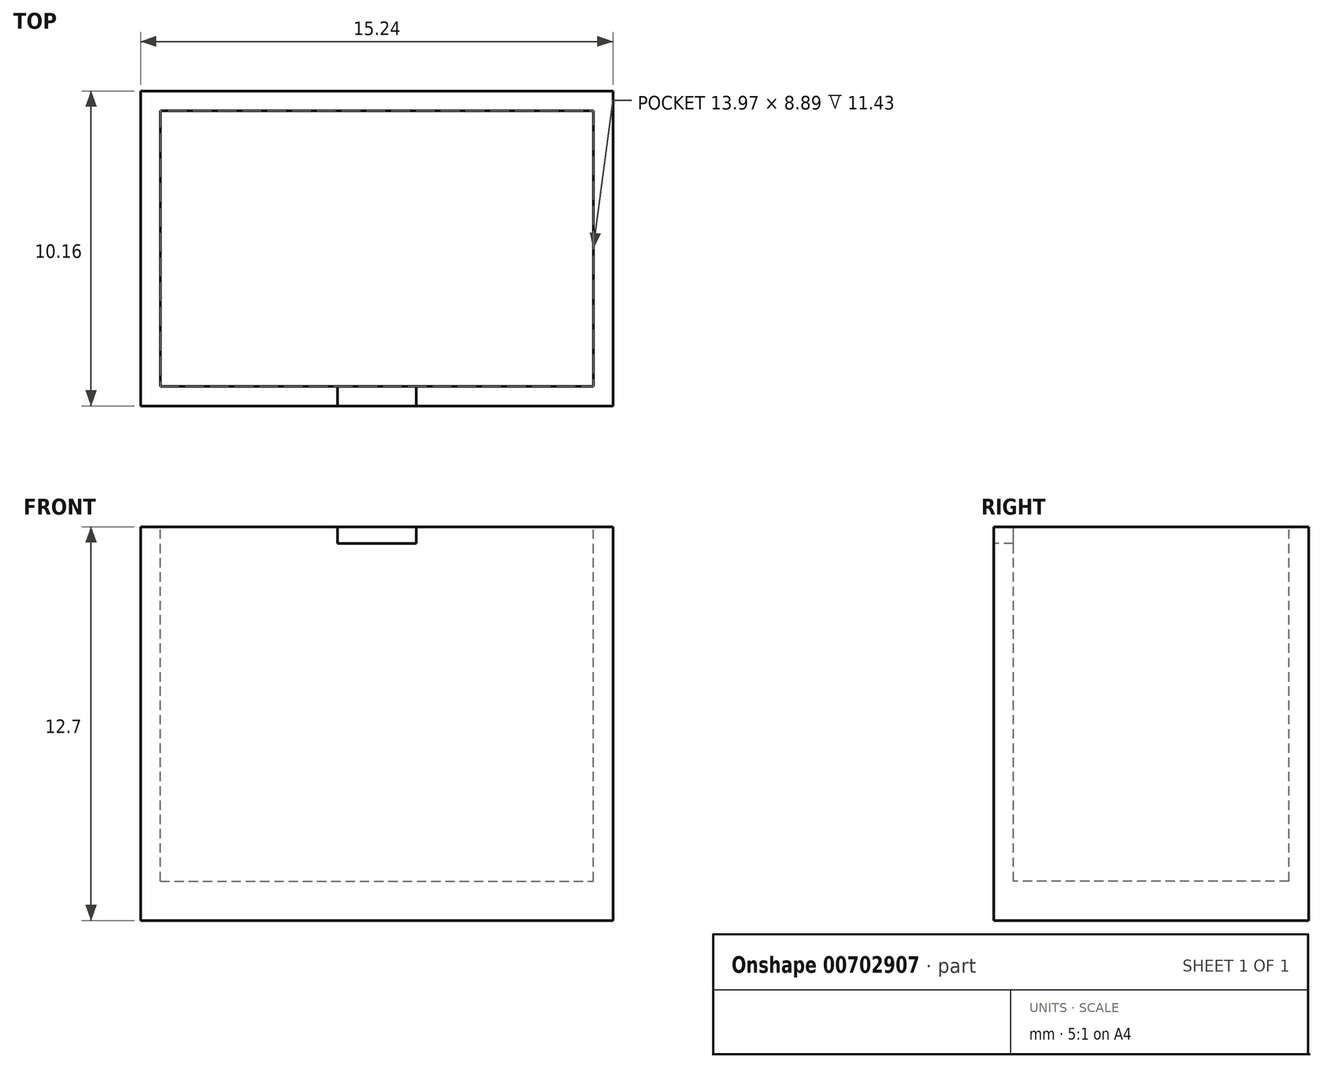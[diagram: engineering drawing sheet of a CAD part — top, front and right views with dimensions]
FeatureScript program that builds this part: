
annotation { "Feature Type Name" : "Feature", "Feature Type Description" : "" }
export const myFeature = defineFeature(function(context is Context, id is Id, definition is map)
    precondition{}
    {
        {
            var Q0;
            Q0=qCreatedBy(makeId("Top.planeOp"),FACE);
            var sketch = newSketch(context, id + "F0", { "sketchPlane" : qUnion([Q0])});
            skLineSegment(sketch, "E0.bottom", {"start": v(-7.62, 5.08) * mm, "end": v(7.62, 5.08) * mm});
            skLineSegment(sketch, "E0.top", {"start": v(-7.62, -5.08) * mm, "end": v(7.62, -5.08) * mm});
            skLineSegment(sketch, "E0.left", {"start": v(-7.62, 5.08) * mm, "end": v(-7.62, -5.08) * mm});
            skLineSegment(sketch, "E0.right", {"start": v(7.62, 5.08) * mm, "end": v(7.62, -5.08) * mm});
            skPoint(sketch, "E0.middle", {"position": v(0, 0) * mm});
            skSolve(sketch);
        }
        {
            var Q0;
            Q0=makeQuery(id+"F0.imprint","IMPRINT",FACE,{"disambiguationData":[TD([[makeQuery(id+"F0.imprint","IMPRINT",EDGE,{"derivedFrom":sQuery(id+"F0.wireOp",EDGE,"E0.bottom")}),-1.0]])]});
            extrude(context, id + "F1", {"entities" : qUnion([Q0]), "depth" : 12.7 * mm, "offsetDistance" : 25.4 * mm});
        }
        {
            var Q0;
            Q0=makeQuery(id+"F1.opExtrude","CAP_FACE",FACE,{"disambiguationData":[OSD([sQuery(id+"F0.wireOp",EDGE,"E0.bottom"),sQuery(id+"F0.wireOp",EDGE,"E0.top"),sQuery(id+"F0.wireOp",EDGE,"E0.left"),sQuery(id+"F0.wireOp",EDGE,"E0.right")])],"isStart":false});
            var sketch = newSketch(context, id + "F2", { "sketchPlane" : qUnion([Q0])});
            skLineSegment(sketch, "E1.bottom", {"start": v(-6.99, 4.45) * mm, "end": v(6.99, 4.45) * mm});
            skLineSegment(sketch, "E1.top", {"start": v(-6.98, -4.45) * mm, "end": v(6.98, -4.45) * mm});
            skLineSegment(sketch, "E1.left", {"start": v(-6.99, 4.45) * mm, "end": v(-6.99, -4.44) * mm});
            skLineSegment(sketch, "E1.right", {"start": v(6.99, 4.45) * mm, "end": v(6.99, -4.44) * mm});
            skPoint(sketch, "E1.middle", {"position": v(0, 0) * mm});
            skSolve(sketch);
        }
        {
            var Q0;
            Q0=makeQuery(id+"F2.imprint","IMPRINT",FACE,{"disambiguationData":[TD([[makeQuery(id+"F2.imprint","IMPRINT",EDGE,{"derivedFrom":sQuery(id+"F2.wireOp",EDGE,"E1.bottom")}),-1.0]])]});
            extrude(context, id + "F3", {"entities" : qUnion([Q0]), "operationType" : NewBodyOperationType.REMOVE, "oppositeDirection" : true, "depth" : 11.43 * mm, "offsetDistance" : 25.4 * mm});
        }
        {
            var Q0;
            Q0=makeQuery(id+"F1.opExtrude","SWEPT_FACE",FACE,{"disambiguationData":[OSD([sQuery(id+"F0.wireOp",EDGE,"E0.top")])]});
            var sketch = newSketch(context, id + "F4", { "sketchPlane" : qUnion([Q0])});
            skLineSegment(sketch, "E2.bottom", {"start": v(-1.27, 12.16) * mm, "end": v(1.27, 12.16) * mm});
            skLineSegment(sketch, "E2.top", {"start": v(-1.27, 13.24) * mm, "end": v(1.27, 13.24) * mm});
            skLineSegment(sketch, "E2.left", {"start": v(-1.27, 12.16) * mm, "end": v(-1.27, 13.24) * mm});
            skLineSegment(sketch, "E2.right", {"start": v(1.27, 12.16) * mm, "end": v(1.27, 13.24) * mm});
            skPoint(sketch, "E2.middle", {"position": v(0, 12.7) * mm});
            skSolve(sketch);
        }
        {
            var Q0;
            {var subQ0=sQuery(id+"F4.wireOp",EDGE,"E2.bottom");Q0=makeQuery(id+"F4.imprint","IMPRINT",FACE,{"disambiguationData":[TD([[makeQuery(id+"F4.imprint","IMPRINT",EDGE,{"derivedFrom":subQ0}),1.0]])]});}
            extrude(context, id + "F5", {"entities" : qUnion([Q0]), "operationType" : NewBodyOperationType.REMOVE, "oppositeDirection" : true, "depth" : 2.54 * mm, "offsetDistance" : 25.4 * mm});
        }
    });
